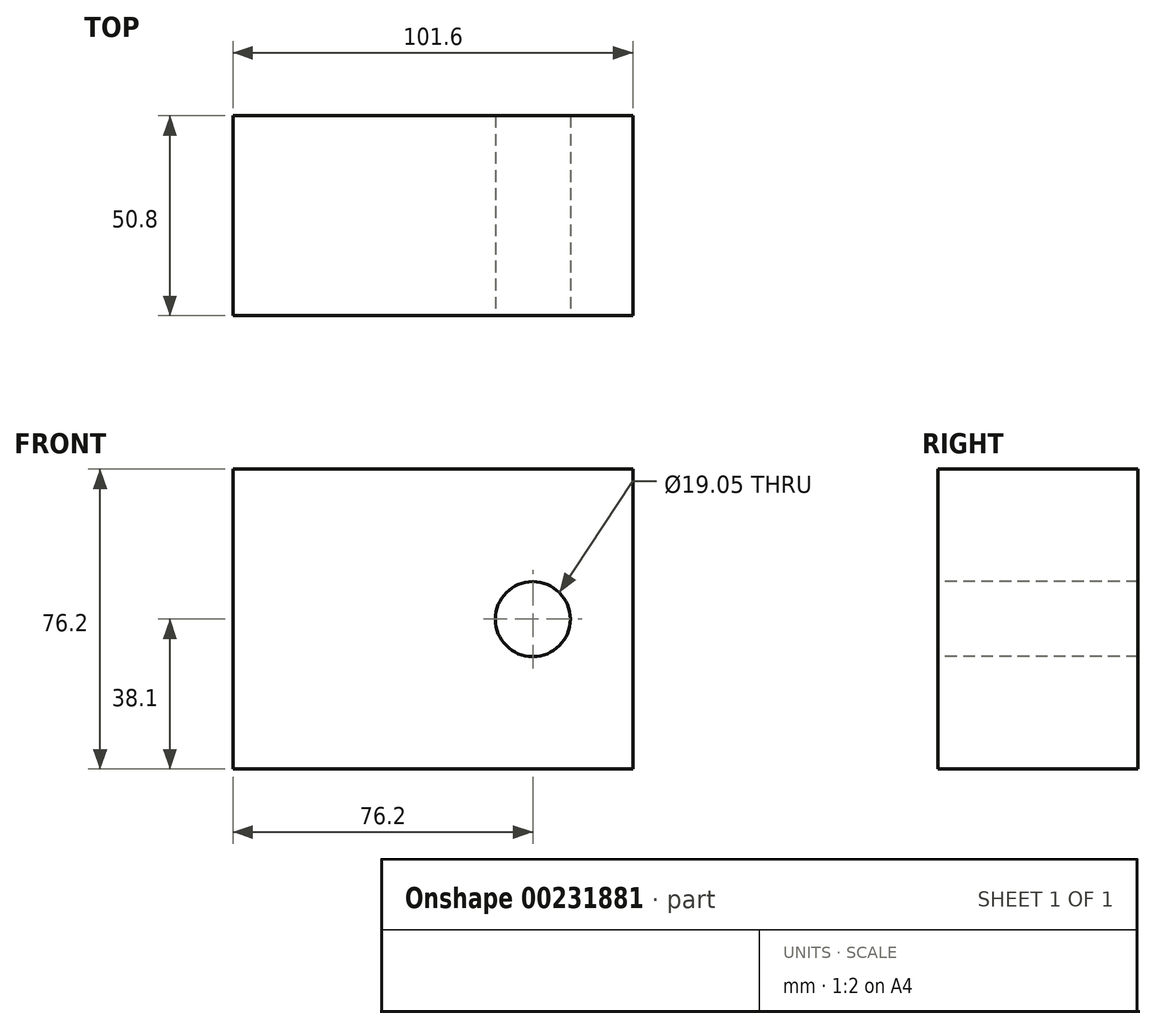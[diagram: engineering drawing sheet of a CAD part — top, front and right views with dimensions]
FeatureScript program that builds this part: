
annotation { "Feature Type Name" : "Feature", "Feature Type Description" : "" }
export const myFeature = defineFeature(function(context is Context, id is Id, definition is map)
    precondition{}
    {
        {
            var Q0;
            Q0=qCreatedBy(makeId("Front.planeOp"),FACE);
            var sketch = newSketch(context, id + "F0", { "sketchPlane" : qUnion([Q0])});
            skLineSegment(sketch, "E0.bottom", {"start": v(0, 0) * mm, "end": v(101.6, 0) * mm});
            skLineSegment(sketch, "E0.top", {"start": v(0, 76.2) * mm, "end": v(101.6, 76.2) * mm});
            skLineSegment(sketch, "E0.left", {"start": v(0, 0) * mm, "end": v(0, 76.2) * mm});
            skLineSegment(sketch, "E0.right", {"start": v(101.6, 0) * mm, "end": v(101.6, 76.2) * mm});
            skSolve(sketch);
        }
        {
            var Q0;
            Q0 = qSketchRegion(id + "F0", true);
            extrude(context, id + "F1", {"entities" : qUnion([Q0]), "depth" : 50.8 * mm});
        }
        {
            var Q0;
            Q0=makeQuery(id+"F1.opExtrude","CAP_FACE",FACE,{"disambiguationData":[OSD([sQuery(id+"F0.wireOp",EDGE,"E0.bottom"),sQuery(id+"F0.wireOp",EDGE,"E0.top"),sQuery(id+"F0.wireOp",EDGE,"E0.left"),sQuery(id+"F0.wireOp",EDGE,"E0.right")])],"isStart":false});
            var sketch = newSketch(context, id + "F2", { "sketchPlane" : qUnion([Q0])});
            skCircle(sketch, "E1", {"center": v(76.2, 38.1) * mm, "radius": 9.53 * mm});
            skSolve(sketch);
        }
        {
            var Q0;
            Q0 = qSketchRegion(id + "F2", true);
            extrude(context, id + "F3", {"entities" : qUnion([Q0]), "operationType" : NewBodyOperationType.REMOVE, "endBound" : BoundingType.UP_TO_NEXT, "oppositeDirection" : true, "depth" : 25.4 * mm});
        }
    });
